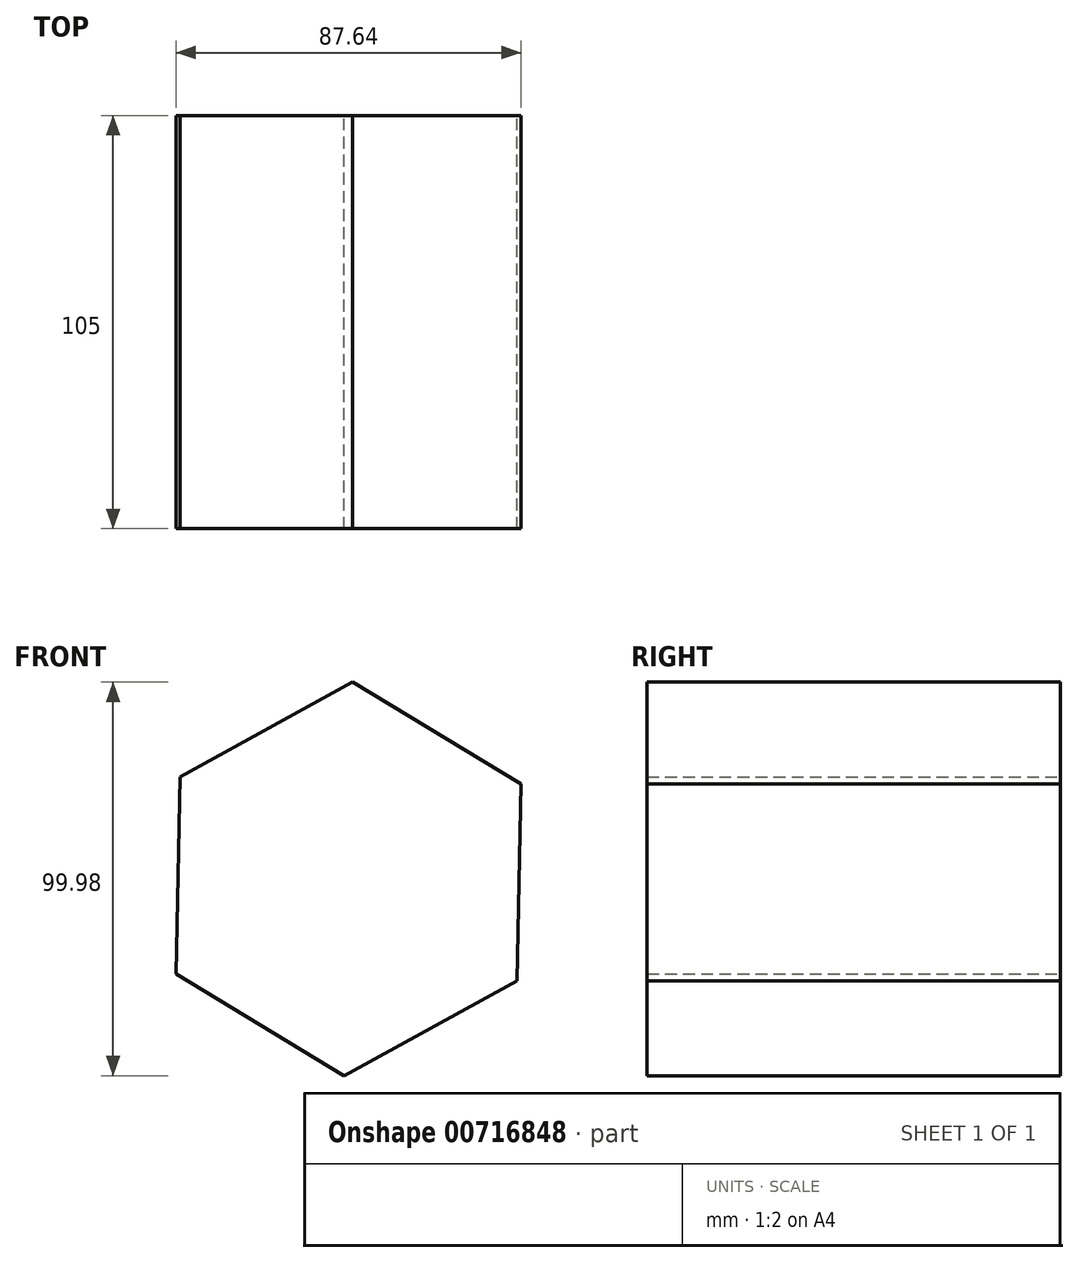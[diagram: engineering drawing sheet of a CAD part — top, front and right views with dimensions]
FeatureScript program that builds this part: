
annotation { "Feature Type Name" : "Feature", "Feature Type Description" : "" }
export const myFeature = defineFeature(function(context is Context, id is Id, definition is map)
    precondition{}
    {
        {
            var Q0;
            Q0=qCreatedBy(makeId("Front.planeOp"),FACE);
            var sketch = newSketch(context, id + "F0", { "sketchPlane" : qUnion([Q0])});
            skCircle(sketch, "E0.cCircle", {"center": v(0, 0) * mm, "radius": 43.3 * mm, "construction": true});
            skLineSegment(sketch, "E0.0", {"start": v(42.76, -25.92) * mm, "end": v(-1.06, -49.99) * mm});
            skLineSegment(sketch, "E0.1", {"start": v(-1.06, -49.99) * mm, "end": v(-43.82, -24.07) * mm});
            skLineSegment(sketch, "E0.2", {"start": v(-43.82, -24.07) * mm, "end": v(-42.76, 25.92) * mm});
            skLineSegment(sketch, "E0.3", {"start": v(-42.76, 25.92) * mm, "end": v(1.06, 49.99) * mm});
            skLineSegment(sketch, "E0.4", {"start": v(1.06, 49.99) * mm, "end": v(43.82, 24.07) * mm});
            skLineSegment(sketch, "E0.5", {"start": v(43.82, 24.07) * mm, "end": v(42.76, -25.92) * mm});
            skPoint(sketch, "E0.0.midPoint", {"position": v(20.85, -37.95) * mm});
            skSolve(sketch);
        }
        {
            var Q0;
            Q0=makeQuery(id+"F0.imprint","IMPRINT",FACE,{"disambiguationData":[TD([[makeQuery(id+"F0.imprint","IMPRINT",EDGE,{"derivedFrom":sQuery(id+"F0.wireOp",EDGE,"E0.0")}),-1.0]])]});
            extrude(context, id + "F1", {"entities" : qUnion([Q0]), "depth" : 105 * mm, "offsetDistance" : 25 * mm});
        }
    });
